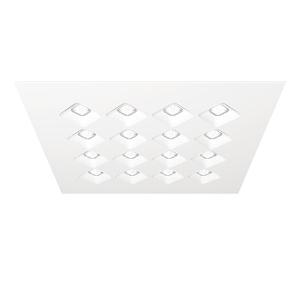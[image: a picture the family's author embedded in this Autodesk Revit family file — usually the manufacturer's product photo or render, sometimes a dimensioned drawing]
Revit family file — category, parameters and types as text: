
# Revit family: 3f_filippi_-_3f_diagon_3f_filippi_-_23410_-_3f_diagon_25w-840_621x621
name_source: partatom
category: Lighting Fixtures
units: mm (PartAtom-declared; Revit-internal decimal feet)

## family parameters
Cut with Voids When Loaded = No
Host = Face
Light Source = No
Part Type = Normal
Room Calculation Point = No
Round Connector Dimension = Use Diameter
Shared = No

## types (1)
- 3F Filippi - 3F Dìagon (1 x LED, 4250 lm, 28 W, 4000 K)
    Apparent Load = 28 VA
    Approval mark = CE
    CIE Flux Codes = 67 96 100 100 100
    Color Rendering = 80
    Color Temperature = 4000 K
    Control Gear = Electronic ballast
    Default Elevation = 1800 mm
    Description = ILLUMINOTECHNICAL
Luminous efficiency 100% (DLOR 100%, ULOR 0%).
Initial luminous flux of the luminaire 4250 lm.
Direct symmetric distribution.
Installation Interdistance Transv.D = 1.39 x hu - Long.D = 1.39 x hu.
Average luminance <1500 cd/m² for radial angles >65°.
Tabular UGR (CIE 117 - 4H-8H; S=0.25H; 70/50/20): RUG 17.3 - 17.3.
Beam angle: 93° - 92°.
Luminous efficacy 152 lm/W.
Lifetime (L95/B10): 30000 h. (tq+25°C)
Lifetime (L90/B10): 50000 h. (tq+25°C)
Lifetime (L80/B10): 80000 h. (tq+25°C)
Lifetime (L75/B10): 100000 h. (tq+25°C)
Sudden decreased luminous flux after 50000 hours: 0% (C0).
Photobiological safety in compliance with IEC/TR 62778: RG0 risk exempt, (IEC 62471).
In compliance with IEC/EN 62722-2-1 - IEC/EN 62717 standards.

SOURCE
Squared LED module 25W/840.
Energy efficiency class (UE 2019/2020 - UE 2019/2015): C.
CIE 13.3 Colour rendering index: CRI >80 (R9 <50%).
IES TM-30 Fidelity Index: Rf = 84 Rg = 95.
CCT nominal colour temperature 4000 K.
Colour initial tolerance (MacAdam): SDCM 3.

MECHANICAL
Housing in hot-galvanised steel, painted in white polyester.
Honeycombed diagonal screen in white anti-glare polycarbonate.
Rhomboidal lenses with differentiated surfaces, etched and prismatic to optimise the orientation of the luminous flux, in transparent methacrylate (PMMA).
Luminaire with limited surface temperature. - D - (EN 60598-2-24)
Dimensions: 621x621 mm, height 30 mm. Weight 3.88 kg.
IP43 protection degree for exposed part, IP20 for recessed part.
Mechanical strength to impacts IK06 (1 joule).
Glow-wire test resistance 650°C.

ELECTRICAL
Halogen Free electronic wiring 230V-50/60Hz, power factor 0.95, THD <25%, constant output current, class I, 1 driver.
Power of the luminaire 28 W.
ENEC - CE.
SAFE FLICKER: PstLM=<1 and SVM=<0.4 (IEC TR 61547-1 and IEC TR 63158), to ensure a more comfortable and safe light.
Luminaire compliant with EN 60598-2-22 for power supply from a centralised emergency system CPSS (Central Power Supply System), not incorporated in the luminaire - high risk areas excluded. The default power and flux are 100% in AC and 100% in DC.
Ambient temperature from 0°C to +25°C.
Temperature class T6 max 85°C.
Quick connection.
Relative humidity UR: <85%.

INSTALLATION
Lay-in recessed fitting.
Height only 30 mm.
Installation on false ceilings with recessed dimensions greater than 596x596 standard size.
Installation after mounting the false ceiling, resting on the exposed structure, minimum void of 140 mm from the lower edge of the structure.
Simultaneous installation with the false ceiling, minimum void of 60 mm from the lower edge of the structure.
All accessories dedicated to this product are available on the Catalog and on our website www.3F-Filippi.com.

APPLICATIONS
Environments: staterooms, with VDTs, offices.
Environments with exacting visual tasks, where diffused soft light for optimum visual comfort is required.

WARNING
Luminaire designed for disposal/recycling at end-of-life.
Replaceable (LED only) light source by a professional. Replaceable control gear by a professional.
    Height = 0 mm  [stored 0 ft]
    Lamp = 1 x LED
    Lamp Light Flux = 4250 lm
    Lamp Power = 28 W
    Lamp count = 1
    Length = 621 mm
    Lifetime = 50000 h
    Luminous efficacy = 152 lm/W
    Manufacturer = 3F Filippi
    ModVariant = No
    Model = 3F Filippi - 23410 - 3F Diagon 25W-840 621x621
    Mounting Place = Ceiling
    Mounting Type = Recessed
    Number of Poles = 1
    OnlyDefault = Yes
    Power Factor = 1
    Product Name = 3F Filippi - 3F Dìagon
    Product group = recessed luminaire
    ProductGroupID = 4
    Protection Class = Protection class I
    Protection Degree = IP 20
    RLX_Detail_Level = 1
    RLX_Emergency_Light_Flux = 0 lm
    RLX_Emergency_Type = 0
    RLX_Emergency_Type_DB = No
    RlxData = <blob elided: 85189 chars, md5=f723bd91>
    Socket = socket
    Standby Power = 0 W
    System Light Flux = 4250 lm
    System Power = 28 W
    Type Comments = Product without accessories
    Type Image = 3ffilippi_3f_diagon.jpg
    URL = http://relux.com
    VarID = ---
    Voltage = 0 V
    Weight = 0.00 kg
    Width = 621 mm

note: [stored X ft] marks values corroborated as IEEE doubles in the binary element streams (Revit-internal decimal feet)

## geometry (parser evidence)
native form markers: Blend x4, Sweep x12
no freeform markers — native parametric forms only
